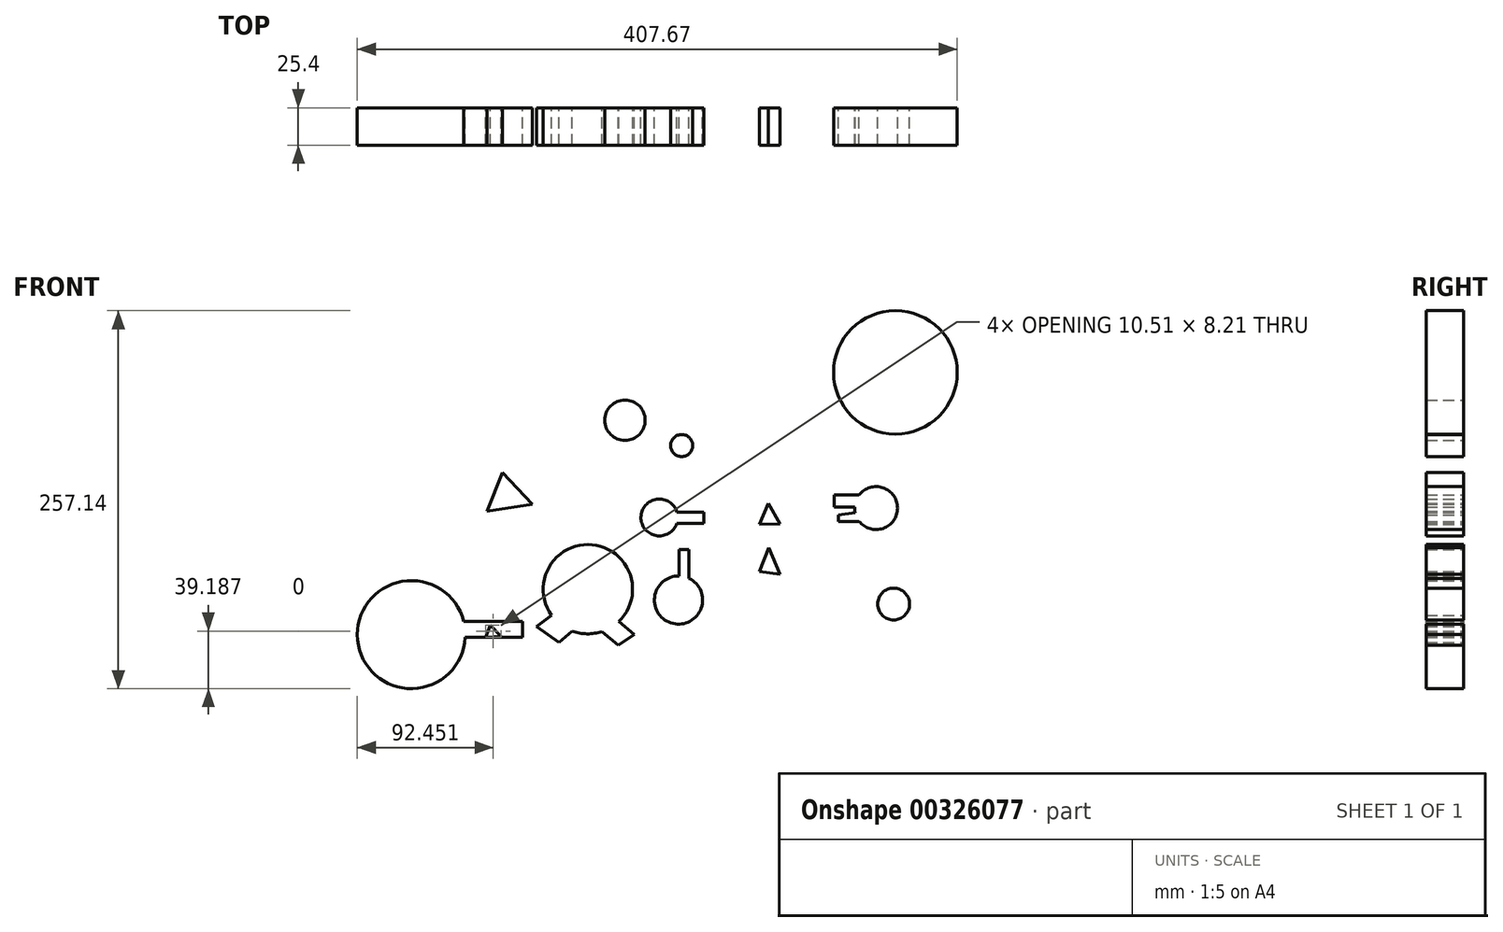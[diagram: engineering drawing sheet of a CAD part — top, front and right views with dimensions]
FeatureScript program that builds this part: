
annotation { "Feature Type Name" : "Feature", "Feature Type Description" : "" }
export const myFeature = defineFeature(function(context is Context, id is Id, definition is map)
    precondition{}
    {
        {
            var Q0;
            Q0=qCreatedBy(makeId("Front.planeOp"),FACE);
            var sketch = newSketch(context, id + "F0", { "sketchPlane" : qUnion([Q0])});
            skCircle(sketch, "E0", {"center": v(0, 14.7) * mm, "radius": 12.53 * mm});
            skLineSegment(sketch, "E1", {"start": v(11.97, 18.37) * mm, "end": v(30.35, 18.37) * mm});
            skLineSegment(sketch, "E2", {"start": v(30.35, 18.37) * mm, "end": v(30.35, 10.54) * mm});
            skLineSegment(sketch, "E3", {"start": v(30.35, 10.54) * mm, "end": v(11.82, 10.54) * mm});
            skLineSegment(sketch, "E4", {"start": v(11.97, 18.37) * mm, "end": v(11.82, 10.54) * mm});
            skLineSegment(sketch, "E5", {"start": v(82.1, 10.22) * mm, "end": v(74.1, 24.28) * mm});
            skLineSegment(sketch, "E6", {"start": v(74.1, 24.28) * mm, "end": v(68.04, 9.9) * mm});
            skLineSegment(sketch, "E7", {"start": v(82.1, 10.22) * mm, "end": v(68.04, 9.9) * mm});
            skLineSegment(sketch, "E8", {"start": v(82.1, 58.46) * mm, "end": v(65.48, 75.39) * mm});
            skLineSegment(sketch, "E9", {"start": v(65.48, 75.39) * mm, "end": v(53.34, 58.77) * mm});
            skLineSegment(sketch, "E10", {"start": v(53.34, 58.77) * mm, "end": v(61.33, 43.44) * mm});
            skLineSegment(sketch, "E11", {"start": v(61.33, 43.44) * mm, "end": v(74.1, 43.44) * mm});
            skLineSegment(sketch, "E12", {"start": v(74.1, 43.44) * mm, "end": v(74.43, 41.85) * mm});
            skLineSegment(sketch, "E13", {"start": v(75.7, 42.48) * mm, "end": v(82.1, 58.46) * mm});
            skLineSegment(sketch, "E14", {"start": v(82.1, -23.96) * mm, "end": v(74.1, -5.43) * mm});
            skLineSegment(sketch, "E15", {"start": v(74.43, -5.43) * mm, "end": v(68.04, -22.04) * mm});
            skLineSegment(sketch, "E16", {"start": v(82.1, -23.96) * mm, "end": v(68.04, -22.04) * mm});
            skLineSegment(sketch, "E17", {"start": v(82.1, -35.14) * mm, "end": v(82.1, -57.82) * mm});
            skLineSegment(sketch, "E18", {"start": v(84, -57.82) * mm, "end": v(68.04, -57.82) * mm});
            skLineSegment(sketch, "E19", {"start": v(68.04, -57.82) * mm, "end": v(70.6, -58.14) * mm});
            skLineSegment(sketch, "E20", {"start": v(69, -56.86) * mm, "end": v(69, -33.22) * mm});
            skLineSegment(sketch, "E21", {"start": v(82.1, -35.14) * mm, "end": v(69, -35.14) * mm});
            skCircle(sketch, "E22", {"center": v(147.27, 21.1) * mm, "radius": 14.6 * mm});
            skLineSegment(sketch, "E23", {"start": v(135.76, 30.09) * mm, "end": v(118.83, 30.09) * mm});
            skLineSegment(sketch, "E24", {"start": v(118.83, 30.09) * mm, "end": v(118.83, 21.72) * mm});
            skLineSegment(sketch, "E25", {"start": v(118.83, 21.72) * mm, "end": v(132.68, 21.72) * mm});
            skLineSegment(sketch, "E26", {"start": v(135.76, 30.09) * mm, "end": v(132.68, 21.72) * mm});
            skLineSegment(sketch, "E27", {"start": v(133, 18.02) * mm, "end": v(135.76, 12.12) * mm});
            skLineSegment(sketch, "E28", {"start": v(135.76, 12.12) * mm, "end": v(121.7, 12.12) * mm});
            skLineSegment(sketch, "E29", {"start": v(121.7, 11.82) * mm, "end": v(121.7, 16.3) * mm});
            skLineSegment(sketch, "E30", {"start": v(121.7, 16.3) * mm, "end": v(133, 18.02) * mm});
            skLineSegment(sketch, "E31", {"start": v(134.8, 17.57) * mm, "end": v(135.76, 21.72) * mm});
            skLineSegment(sketch, "E32", {"start": v(135.76, 21.72) * mm, "end": v(134.8, 17.57) * mm});
            skLineSegment(sketch, "E33", {"start": v(145.48, -25.85) * mm, "end": v(162.72, -39.81) * mm});
            skLineSegment(sketch, "E34", {"start": v(162.72, -39.81) * mm, "end": v(159.2, -44.16) * mm});
            skLineSegment(sketch, "E35", {"start": v(159.2, -44.16) * mm, "end": v(142.77, -30.87) * mm});
            skLineSegment(sketch, "E36", {"start": v(143.29, -30.23) * mm, "end": v(145.48, -25.85) * mm});
            skCircle(sketch, "E37", {"center": v(159.2, -44.16) * mm, "radius": 10.84 * mm});
            skCircle(sketch, "E38", {"center": v(-23.36, 80.87) * mm, "radius": 13.74 * mm});
            skLineSegment(sketch, "E39", {"start": v(-9.8, 78.66) * mm, "end": v(5.65, 69.65) * mm});
            skLineSegment(sketch, "E40", {"start": v(6.2, 69.37) * mm, "end": v(-4.2, 58.98) * mm});
            skLineSegment(sketch, "E41", {"start": v(-4.2, 58.98) * mm, "end": v(-19.1, 67.8) * mm});
            skLineSegment(sketch, "E42", {"start": v(-19.1, 67.8) * mm, "end": v(-19.1, 75.12) * mm});
            skLineSegment(sketch, "E43", {"start": v(-18.7, 75.12) * mm, "end": v(-22, 71.84) * mm});
            skCircle(sketch, "E44", {"center": v(15.22, 63.63) * mm, "radius": 7.51 * mm});
            skCircle(sketch, "E45", {"center": v(-48.54, -34.06) * mm, "radius": 30.36 * mm});
            skLineSegment(sketch, "E46", {"start": v(-21.84, -19.6) * mm, "end": v(-10.77, -10.26) * mm});
            skLineSegment(sketch, "E47", {"start": v(-10.77, -10.26) * mm, "end": v(-28.29, 5.61) * mm});
            skLineSegment(sketch, "E48", {"start": v(-28.29, 5.89) * mm, "end": v(-38.94, -5.26) * mm});
            skLineSegment(sketch, "E49", {"start": v(-59.15, -62.5) * mm, "end": v(-68.24, -70.18) * mm});
            skLineSegment(sketch, "E50", {"start": v(-68.24, -70.18) * mm, "end": v(-83.29, -59.51) * mm});
            skLineSegment(sketch, "E51", {"start": v(-83.29, -59.51) * mm, "end": v(-73.17, -51.8) * mm});
            skLineSegment(sketch, "E52", {"start": v(-73.17, -51.8) * mm, "end": v(-74.53, -52.67) * mm});
            skLineSegment(sketch, "E53", {"start": v(-27.68, -56.12) * mm, "end": v(-17.07, -64.99) * mm});
            skLineSegment(sketch, "E54", {"start": v(-17.07, -64.99) * mm, "end": v(-27.74, -72.1) * mm});
            skLineSegment(sketch, "E55", {"start": v(-27.74, -72.1) * mm, "end": v(-38.94, -62.86) * mm});
            skLineSegment(sketch, "E56", {"start": v(-61.34, -6.54) * mm, "end": v(-78.09, 7.26) * mm});
            skLineSegment(sketch, "E57", {"start": v(-78.09, 7.26) * mm, "end": v(-92.51, -10.26) * mm});
            skLineSegment(sketch, "E58", {"start": v(-92.87, -10.53) * mm, "end": v(-76.12, -21.38) * mm});
            skLineSegment(sketch, "E59", {"start": v(-105.73, -38.99) * mm, "end": v(-118.04, -17.37) * mm});
            skLineSegment(sketch, "E60", {"start": v(-118.04, -17.37) * mm, "end": v(-123.51, -36.25) * mm});
            skLineSegment(sketch, "E61", {"start": v(-120.23, -36.25) * mm, "end": v(-105.73, -38.99) * mm});
            skLineSegment(sketch, "E62", {"start": v(-105.73, -68.27) * mm, "end": v(-114.76, -58.42) * mm});
            skLineSegment(sketch, "E63", {"start": v(-114.76, -58.42) * mm, "end": v(-118.04, -66.63) * mm});
            skLineSegment(sketch, "E64", {"start": v(-118.04, -66.63) * mm, "end": v(-107.54, -66.3) * mm});
            skLineSegment(sketch, "E65", {"start": v(-85.2, 22.58) * mm, "end": v(-107.54, 46.39) * mm});
            skLineSegment(sketch, "E66", {"start": v(-106.28, 46.39) * mm, "end": v(-117.22, 19.02) * mm});
            skLineSegment(sketch, "E67", {"start": v(-117.22, 19.02) * mm, "end": v(-86.37, 23.82) * mm});
            skLineSegment(sketch, "E68", {"start": v(-81.37, 119.45) * mm, "end": v(-83.56, 81.14) * mm});
            skLineSegment(sketch, "E69", {"start": v(-83.56, 81.14) * mm, "end": v(-102.9, 82.24) * mm});
            skLineSegment(sketch, "E70", {"start": v(-103.54, 80.6) * mm, "end": v(-99.43, 108.78) * mm});
            skLineSegment(sketch, "E71", {"start": v(-99.43, 108.78) * mm, "end": v(-81.37, 119.45) * mm});
            skLineSegment(sketch, "E72", {"start": v(22.1, 60.6) * mm, "end": v(41.22, 45.84) * mm});
            skLineSegment(sketch, "E73", {"start": v(41.5, 45.84) * mm, "end": v(31.92, 36.26) * mm});
            skLineSegment(sketch, "E74", {"start": v(31.92, 36.26) * mm, "end": v(9.9, 58.32) * mm});
            skCircle(sketch, "E75", {"center": v(13.03, -41.45) * mm, "radius": 16.4 * mm});
            skLineSegment(sketch, "E76", {"start": v(13.36, -25.06) * mm, "end": v(13.36, -6.97) * mm});
            skLineSegment(sketch, "E77", {"start": v(13.36, -6.97) * mm, "end": v(20.15, -6.97) * mm});
            skLineSegment(sketch, "E78", {"start": v(20.15, -6.43) * mm, "end": v(20.15, -26.68) * mm});
            skLineSegment(sketch, "E79", {"start": v(13.36, -6.97) * mm, "end": v(8.1, -6.97) * mm});
            skLineSegment(sketch, "E80", {"start": v(8.1, -7.52) * mm, "end": v(8.1, -25.82) * mm});
            skCircle(sketch, "E81", {"center": v(160.42, 113.42) * mm, "radius": 42 * mm});
            skLineSegment(sketch, "E82", {"start": v(119.27, 121.85) * mm, "end": v(0, 121.85) * mm});
            skLineSegment(sketch, "E83", {"start": v(-0.57, 122.46) * mm, "end": v(-0.57, 109.33) * mm});
            skLineSegment(sketch, "E84", {"start": v(-1.34, 109.33) * mm, "end": v(118.61, 109.33) * mm});
            skLineSegment(sketch, "E85", {"start": v(115.53, 109.6) * mm, "end": v(206.47, 109.6) * mm});
            skLineSegment(sketch, "E86", {"start": v(206.47, 109.6) * mm, "end": v(206.47, 107.96) * mm});
            skLineSegment(sketch, "E87", {"start": v(206.47, 107.96) * mm, "end": v(206.47, 124.92) * mm});
            skCircle(sketch, "E88", {"center": v(-168.52, -65) * mm, "radius": 36.72 * mm});
            skLineSegment(sketch, "E89", {"start": v(-132.93, -56) * mm, "end": v(-93.06, -56) * mm});
            skLineSegment(sketch, "E90", {"start": v(-93.06, -54.86) * mm, "end": v(-93.06, -66.9) * mm});
            skLineSegment(sketch, "E91", {"start": v(-93.06, -66.9) * mm, "end": v(-91.51, -66.9) * mm});
            skLineSegment(sketch, "E92", {"start": v(-91.51, -66.9) * mm, "end": v(-131.85, -66.9) * mm});
            skSolve(sketch);
        }
        {
            var Q0;
            Q0 = qSketchRegion(id + "F0", true);
            extrude(context, id + "F1", {"entities" : qUnion([Q0]), "depth" : 25.4 * mm});
        }
        {
            var Q0;
            Q0 = qSketchRegion(id + "F0", true);
            extrude(context, id + "F2", {"entities" : qUnion([Q0]), "operationType" : NewBodyOperationType.ADD, "depth" : 25.4 * mm});
        }
        {
            var Q0;
            Q0 = qSketchRegion(id + "F0", true);
            extrude(context, id + "F3", {"entities" : qUnion([Q0]), "depth" : 25.4 * mm});
        }
        {
            var Q0;
            Q0 = qSketchRegion(id + "F0", true);
            extrude(context, id + "F4", {"entities" : qUnion([Q0]), "depth" : 25.4 * mm});
        }
        {
            var Q0;
            Q0 = qSketchRegion(id + "F0", true);
            extrude(context, id + "F5", {"entities" : qUnion([Q0]), "depth" : 25.4 * mm});
        }
    });
